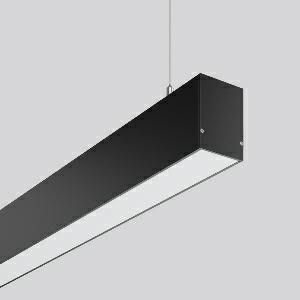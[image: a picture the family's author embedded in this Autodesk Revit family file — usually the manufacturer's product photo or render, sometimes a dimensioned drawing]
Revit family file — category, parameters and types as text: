
# Revit family: less_is_more_50_312317_003_76_112b
name_source: partatom
category: Lighting Fixtures
units: mm (PartAtom-declared; Revit-internal decimal feet)

## family parameters
Cut with Voids When Loaded = No
Host = Face
Light Source = No
Part Type = Normal
Room Calculation Point = No
Round Connector Dimension = Use Diameter
Shared = No

## types (1)
- LESS IS MORE 50 (1 x LED Modul 830, 3850 lm, 3000)
    Apparent Load = 34 VA
    CIE Flux Codes = 49 80 96 63 100
    Color Rendering = 80
    Color Temperature = 3000
    Default Elevation = 1800 mm
    Description = Series: LESS IS MORE 50
Linear pendant luminaire for aesthetically sophisticated lighting. Housing: extruded aluminium profile, powder-coated. End cap aluminium powder-coated. Canopy made of aluminium, powder-coated. Diffuser made of non-yellowing plastic (PMMA), opal. Direct 65%, indirect 35% light emission. Suitable for pendant. 2-point steel cable suspension freely positionable and infinitely height-adjustable. Special lengths available on request. LED unit with integrated converter interchangeable and removable. Suitable for through-wiring. With sensors or as a safety luminaire on request. 
Colour: deep black, matt (RAL 9005)
Length: 847 mm
Width: 57 mm
Height: 75 mm
Suspension length: 2000 mm
Lamp: LED
Socket: without socket
Colour temperature: 3000K
Colour rendering index (CRI): 80
Light source: LED
Socket lamp2: Without base
Colour temperature: 3000K
System power: 34 W
Rated luminous flux: 3850 lm
Luminous efficiency: 113 lm/W
Control gear: Converter, dimmable, DALI
Control gear: Converter, dimmable, DALI
Protection class: I
Type of protection: IP 20
    Height = 75 mm
    Lamp = 1 x LED Modul 830
    Lamp Light Flux = 3850 lm
    Lamp count = 1
    Length = 847 mm
    Lifetime = 50000 h
    Luminous efficacy = 113 lm/W
    Manufacturer = RZB
    ModVariant = No
    Model = 312317.003.76
    Mounting Place = Ceiling
    Mounting Type = Pendant
    Number of Poles = 1
    OnlyDefault = Yes
    Power Factor = 1
    Product Name = LESS IS MORE 50
    Product group = Pendant LED linear luminaires
    ProductGroupID = 907
    Protection Class = Protection class I
    Protection Degree = IP 20
    RLX_Detail_Level = 1
    RLX_Emergency_Light_Flux = 0 lm
    RLX_Emergency_Type = 0
    RLX_Emergency_Type_DB = No
    RlxData = <blob elided: 39873 chars, md5=369e8627>
    Socket = socket
    Standby Power = 0 W
    System Light Flux = 3850 lm
    System Power = 34 W
    Type Comments = Product without accessories
    Type Image = 312318.003.jpg
    URL = http://relux.com
    VarID = ---
    Voltage = 230 V
    Voltage Range = 220-240 V
    Weight = 0.00 kg
    Width = 57 mm

## geometry (parser evidence)
native form markers: Blend x4, Sweep x13
no freeform markers — native parametric forms only
